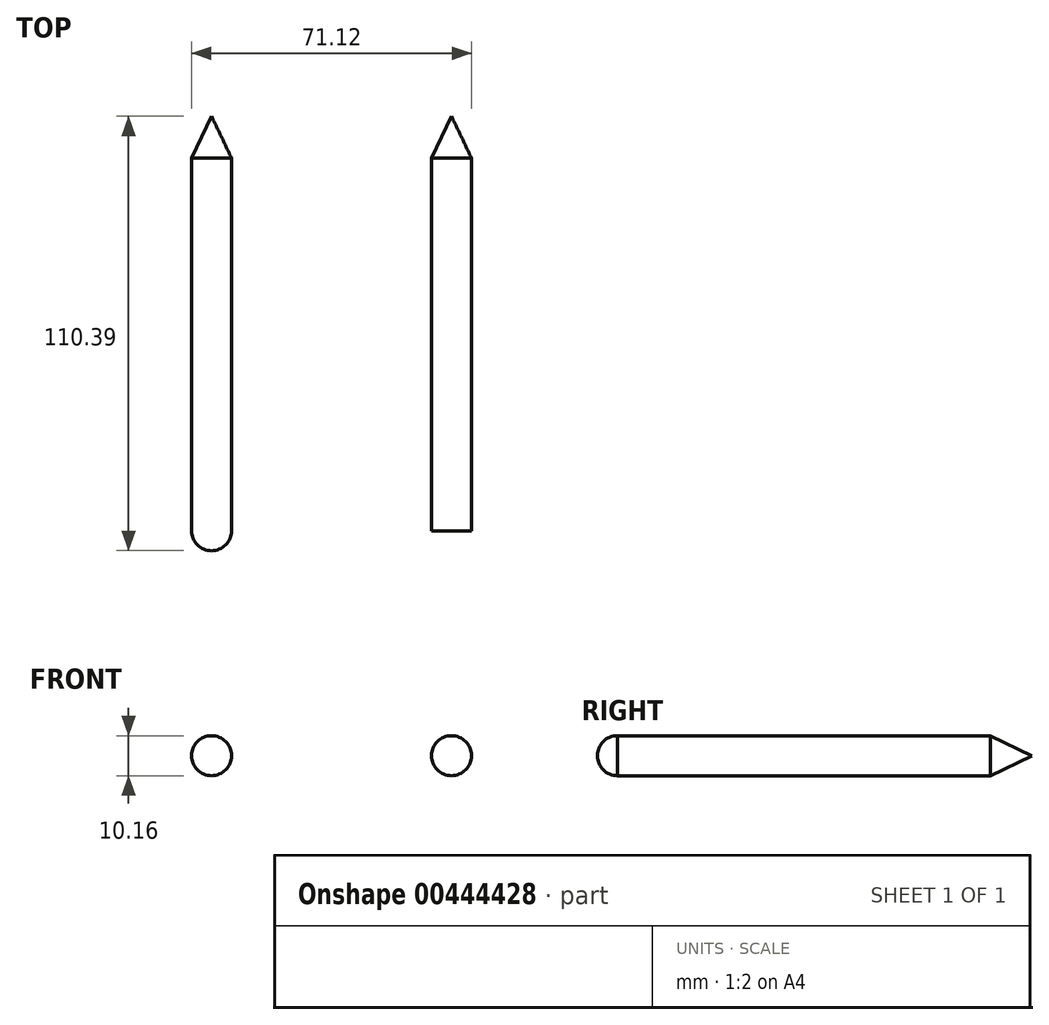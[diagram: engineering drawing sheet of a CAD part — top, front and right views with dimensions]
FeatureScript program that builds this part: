
annotation { "Feature Type Name" : "Feature", "Feature Type Description" : "" }
export const myFeature = defineFeature(function(context is Context, id is Id, definition is map)
    precondition{}
    {
        {
            var Q0;
            Q0=qCreatedBy(makeId("Top.planeOp"),FACE);
            var sketch = newSketch(context, id + "F0", { "sketchPlane" : qUnion([Q0])});
            skLineSegment(sketch, "E0.bottom", {"start": v(27.22, 47.35) * mm, "end": v(-23.58, 47.35) * mm});
            skLineSegment(sketch, "E0.left", {"start": v(27.22, 47.35) * mm, "end": v(27.22, -47.35) * mm});
            skLineSegment(sketch, "E0.right", {"start": v(-23.58, 47.35) * mm, "end": v(-23.58, -47.35) * mm});
            skPoint(sketch, "E0.middle", {"position": v(1.82, 0) * mm});
            skLineSegment(sketch, "E1", {"start": v(-33.74, 47.35) * mm, "end": v(-33.74, -47.35) * mm});
            skLineSegment(sketch, "E2", {"start": v(-33.74, -47.35) * mm, "end": v(-23.58, -47.35) * mm});
            skLineSegment(sketch, "E3", {"start": v(37.38, 47.35) * mm, "end": v(37.38, -47.35) * mm});
            skLineSegment(sketch, "E4", {"start": v(37.38, -47.35) * mm, "end": v(27.22, -47.35) * mm});
            skArc(sketch, "E5", {"start": v(-33.74, -47.35) * mm, "mid": v(-28.66, -52.43) * mm, "end": v(-23.58, -47.35) * mm});
            skArc(sketch, "E6", {"start": v(27.22, -47.35) * mm, "mid": v(32.3, -52.43) * mm, "end": v(37.38, -47.35) * mm});
            skArc(sketch, "E7", {"start": v(-23.58, -47.35) * mm, "mid": v(1.82, -60.1) * mm, "end": v(27.22, -47.35) * mm});
            skLineSegment(sketch, "E8", {"start": v(-28.66, 47.35) * mm, "end": v(-28.66, 57.96) * mm});
            skPoint(sketch, "E9.endSnap0", {"position": v(32.3, 47.35) * mm});
            skLineSegment(sketch, "E10", {"start": v(32.3, 57.96) * mm, "end": v(32.3, 47.35) * mm});
            skLineSegment(sketch, "E11", {"start": v(-28.66, 57.96) * mm, "end": v(-33.74, 47.35) * mm});
            skLineSegment(sketch, "E12", {"start": v(-28.66, 57.96) * mm, "end": v(-23.58, 47.35) * mm});
            skLineSegment(sketch, "E13", {"start": v(32.3, 57.96) * mm, "end": v(27.22, 47.35) * mm});
            skLineSegment(sketch, "E14", {"start": v(32.3, 57.96) * mm, "end": v(37.38, 47.35) * mm});
            skLineSegment(sketch, "E15", {"start": v(-28.66, -47.35) * mm, "end": v(-28.66, 47.35) * mm});
            skLineSegment(sketch, "E16", {"start": v(32.3, 47.35) * mm, "end": v(32.3, -47.35) * mm});
            skSolve(sketch);
        }
        {
            var Q0;
            {var subQ1=sQuery(id+"F0.wireOp",EDGE,"E0.right");Q0=makeQuery(id+"F0.imprint","IMPRINT",FACE,{"disambiguationData":[TD([[makeQuery(id+"F0.imprint","IMPRINT",EDGE,{"derivedFrom":subQ1}),-1.0]])]});}
            var Q1;
            Q1=sQuery(id+"F0.wireOp",EDGE,"E15");
            revolve(context, id + "F1", {"entities" : qUnion([Q0]), "axis" : qUnion([Q1]), "revolveType" : RevolveType.FULL});
        }
        {
            var Q0;
            {var subQ1=sQuery(id+"F0.wireOp",EDGE,"E0.left");Q0=makeQuery(id+"F0.imprint","IMPRINT",FACE,{"disambiguationData":[TD([[makeQuery(id+"F0.imprint","IMPRINT",EDGE,{"derivedFrom":subQ1}),1.0]])]});}
            var Q1;
            Q1=sQuery(id+"F0.wireOp",EDGE,"E16");
            revolve(context, id + "F2", {"entities" : qUnion([Q0]), "axis" : qUnion([Q1]), "revolveType" : RevolveType.FULL});
        }
        {
            var Q0;
            Q0=sQuery(id+"F0.wireOp",EDGE,"E6");
            var Q1;
            Q1=sQuery(id+"F0.wireOp",EDGE,"E4");
            revolve(context, id + "F3", {"bodyType" : ToolBodyType.SURFACE, "surfaceEntities" : qUnion([Q0]), "axis" : qUnion([Q1]), "revolveType" : RevolveType.FULL});
        }
        {
            var Q0;
            {var subQ0=sQuery(id+"F0.wireOp",EDGE,"E5");Q0=makeQuery(id+"F0.imprint","IMPRINT",FACE,{"disambiguationData":[TD([[makeQuery(id+"F0.imprint","IMPRINT",EDGE,{"derivedFrom":subQ0}),1.0]])]});}
            var Q1;
            Q1=sQuery(id+"F0.wireOp",EDGE,"E2");
            revolve(context, id + "F4", {"operationType" : NewBodyOperationType.ADD, "entities" : qUnion([Q0]), "axis" : qUnion([Q1]), "revolveType" : RevolveType.FULL});
        }
    });
